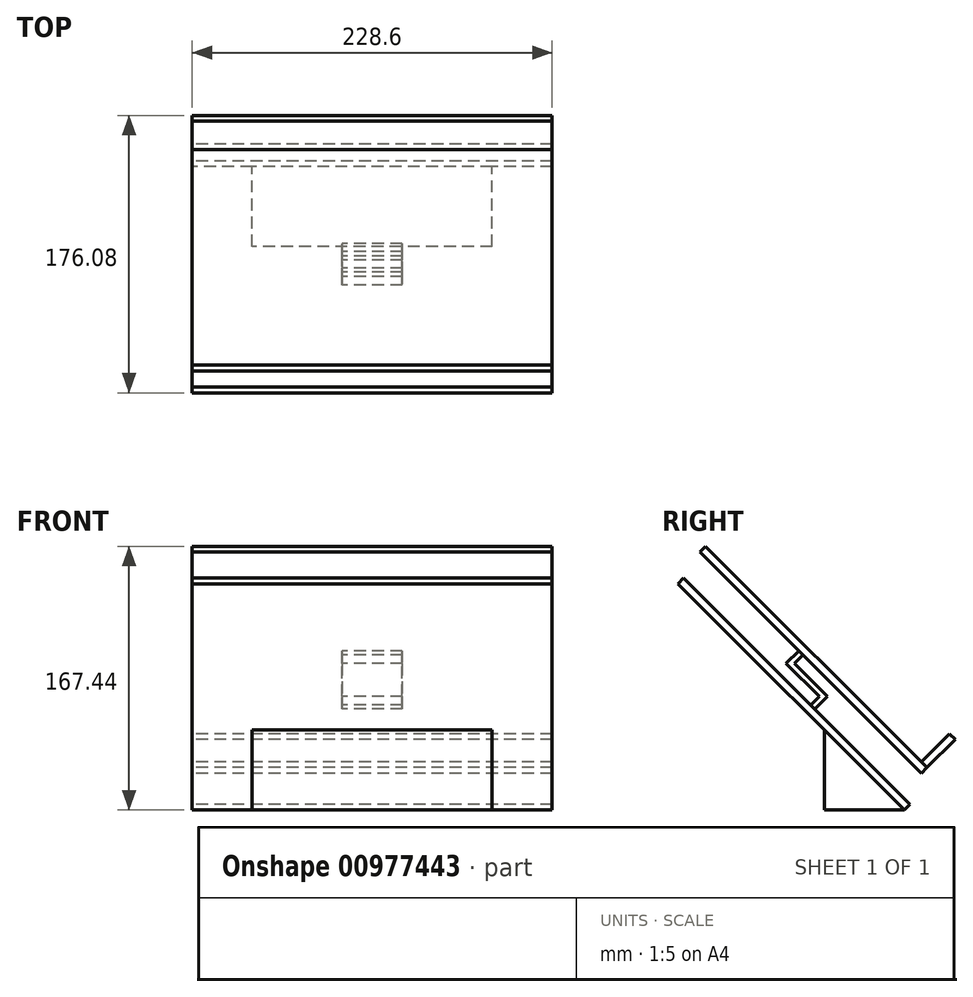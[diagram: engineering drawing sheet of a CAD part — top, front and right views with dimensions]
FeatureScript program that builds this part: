
annotation { "Feature Type Name" : "Feature", "Feature Type Description" : "" }
export const myFeature = defineFeature(function(context is Context, id is Id, definition is map)
    precondition{}
    {
        {
            var Q0;
            Q0=qCreatedBy(makeId("Right.planeOp"),FACE);
            var sketch = newSketch(context, id + "F0", { "sketchPlane" : qUnion([Q0])});
            skLineSegment(sketch, "E0", {"start": v(50.8, 0) * mm, "end": v(0, 50.8) * mm});
            skLineSegment(sketch, "E1", {"start": v(0, 50.8) * mm, "end": v(0, 0) * mm});
            skLineSegment(sketch, "E2", {"start": v(0, 0) * mm, "end": v(50.8, 0) * mm});
            skSolve(sketch);
        }
        {
            var Q0;
            Q0 = qSketchRegion(id + "F0", true);
            extrude(context, id + "F1", {"entities" : qUnion([Q0]), "endBound" : BoundingType.SYMMETRIC, "depth" : 152.4 * mm, "offsetDistance" : 25.4 * mm});
        }
        {
            var Q0;
            Q0=qCreatedBy(makeId("Right.planeOp"),FACE);
            var sketch = newSketch(context, id + "F2", { "sketchPlane" : qUnion([Q0])});
            skLineSegment(sketch, "E3", {"start": v(50.8, 0) * mm, "end": v(-92.88, 143.68) * mm});
            skLineSegment(sketch, "E4", {"start": v(-92.88, 143.68) * mm, "end": v(-89.3, 147.28) * mm});
            skLineSegment(sketch, "E5", {"start": v(-89.3, 147.28) * mm, "end": v(54.4, 3.6) * mm});
            skLineSegment(sketch, "E6", {"start": v(54.4, 3.6) * mm, "end": v(50.8, 0) * mm});
            skSolve(sketch);
        }
        {
            var Q0;
            Q0 = qSketchRegion(id + "F2", true);
            extrude(context, id + "F3", {"entities" : qUnion([Q0]), "operationType" : NewBodyOperationType.ADD, "endBound" : BoundingType.SYMMETRIC, "depth" : 228.6 * mm, "offsetDistance" : 25.4 * mm});
        }
        {
            var Q0;
            Q0=qCreatedBy(makeId("Right.planeOp"),FACE);
            var sketch = newSketch(context, id + "F4", { "sketchPlane" : qUnion([Q0])});
            skLineSegment(sketch, "E7", {"start": v(-13.63, 98.55) * mm, "end": v(-16.2, 101.13) * mm});
            skLineSegment(sketch, "E8", {"start": v(-16.2, 101.13) * mm, "end": v(-24.29, 93.05) * mm});
            skLineSegment(sketch, "E9", {"start": v(-24.29, 93.05) * mm, "end": v(-3.2, 71.97) * mm});
            skLineSegment(sketch, "E10", {"start": v(-3.2, 71.97) * mm, "end": v(-8.6, 66.58) * mm});
            skLineSegment(sketch, "E11", {"start": v(-8.6, 66.58) * mm, "end": v(-6.02, 64) * mm});
            skLineSegment(sketch, "E12", {"start": v(-6.02, 64) * mm, "end": v(2.07, 72.08) * mm});
            skLineSegment(sketch, "E13", {"start": v(2.07, 72.08) * mm, "end": v(-19.01, 93.16) * mm});
            skLineSegment(sketch, "E14", {"start": v(-19.01, 93.16) * mm, "end": v(-13.63, 98.55) * mm});
            skSolve(sketch);
        }
        {
            var Q0;
            Q0 = qSketchRegion(id + "F4", true);
            extrude(context, id + "F5", {"entities" : qUnion([Q0]), "operationType" : NewBodyOperationType.ADD, "endBound" : BoundingType.SYMMETRIC, "depth" : 38.1 * mm, "offsetDistance" : 25.4 * mm});
        }
        {
            var Q0;
            Q0=qCreatedBy(makeId("Right.planeOp"),FACE);
            var sketch = newSketch(context, id + "F6", { "sketchPlane" : qUnion([Q0])});
            skLineSegment(sketch, "E15", {"start": v(-78.92, 163.85) * mm, "end": v(-75.33, 167.44) * mm});
            skLineSegment(sketch, "E16", {"start": v(-75.33, 167.44) * mm, "end": v(65.24, 26.87) * mm});
            skLineSegment(sketch, "E17", {"start": v(65.24, 26.87) * mm, "end": v(61.64, 23.28) * mm});
            skLineSegment(sketch, "E18", {"start": v(61.64, 23.28) * mm, "end": v(-78.92, 163.85) * mm});
            skSolve(sketch);
        }
        {
            var Q0;
            Q0 = qSketchRegion(id + "F6", true);
            extrude(context, id + "F7", {"entities" : qUnion([Q0]), "operationType" : NewBodyOperationType.ADD, "endBound" : BoundingType.SYMMETRIC, "depth" : 228.6 * mm, "offsetDistance" : 25.4 * mm});
        }
        {
            var Q0;
            Q0=qCreatedBy(makeId("Right.planeOp"),FACE);
            var sketch = newSketch(context, id + "F8", { "sketchPlane" : qUnion([Q0])});
            skLineSegment(sketch, "E19", {"start": v(61.64, 30.46) * mm, "end": v(65.24, 26.87) * mm});
            skLineSegment(sketch, "E20", {"start": v(65.24, 26.87) * mm, "end": v(83.2, 44.83) * mm});
            skLineSegment(sketch, "E21", {"start": v(83.2, 44.83) * mm, "end": v(79.6, 48.43) * mm});
            skLineSegment(sketch, "E22", {"start": v(79.6, 48.43) * mm, "end": v(61.64, 30.46) * mm});
            skSolve(sketch);
        }
        {
            var Q0;
            Q0 = qSketchRegion(id + "F8", true);
            extrude(context, id + "F9", {"entities" : qUnion([Q0]), "endBound" : BoundingType.SYMMETRIC, "depth" : 228.6 * mm, "offsetDistance" : 25.4 * mm});
        }
    });
